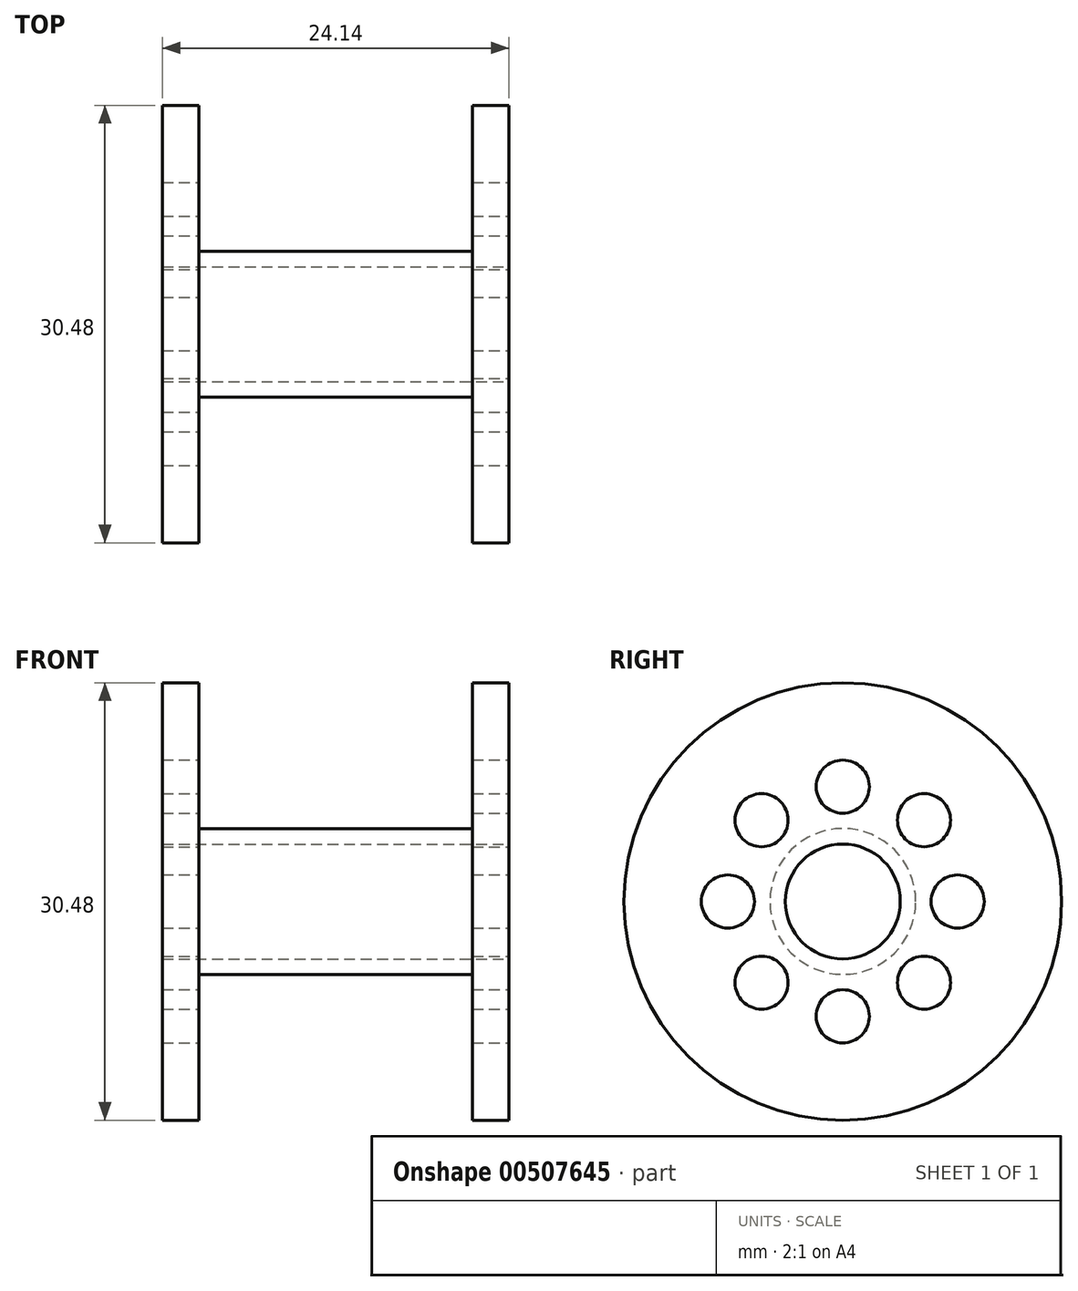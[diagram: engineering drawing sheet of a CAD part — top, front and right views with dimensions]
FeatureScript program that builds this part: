
annotation { "Feature Type Name" : "Feature", "Feature Type Description" : "" }
export const myFeature = defineFeature(function(context is Context, id is Id, definition is map)
    precondition{}
    {
        {
            var Q0;
            Q0=qCreatedBy(makeId("Top.planeOp"),FACE);
            var sketch = newSketch(context, id + "F0", { "sketchPlane" : qUnion([Q0])});
            skLineSegment(sketch, "E0.bottom", {"start": v(-9.53, 5.08) * mm, "end": v(9.53, 5.08) * mm});
            skLineSegment(sketch, "E0.left", {"start": v(-9.53, 5.08) * mm, "end": v(-9.53, 0) * mm});
            skLineSegment(sketch, "E0.right", {"start": v(9.53, 5.08) * mm, "end": v(9.53, 0) * mm});
            skPoint(sketch, "E0.middle", {"position": v(0, 0) * mm});
            skLineSegment(sketch, "E1.bottom", {"start": v(-9.53, 0) * mm, "end": v(-12.07, 0) * mm});
            skLineSegment(sketch, "E1.top", {"start": v(-9.53, 15.24) * mm, "end": v(-12.07, 15.24) * mm});
            skLineSegment(sketch, "E1.left", {"start": v(-9.53, 5.08) * mm, "end": v(-9.53, 15.24) * mm});
            skLineSegment(sketch, "E1.right", {"start": v(-12.07, 0) * mm, "end": v(-12.07, 15.24) * mm});
            skLineSegment(sketch, "E2.bottom", {"start": v(9.53, 0) * mm, "end": v(12.07, 0) * mm});
            skLineSegment(sketch, "E2.top", {"start": v(9.53, 15.24) * mm, "end": v(12.06, 15.24) * mm});
            skLineSegment(sketch, "E2.left", {"start": v(9.53, 0) * mm, "end": v(9.53, 15.24) * mm});
            skLineSegment(sketch, "E2.right", {"start": v(12.07, 0) * mm, "end": v(12.06, 15.24) * mm});
            skPoint(sketch, "E3.orphan", {"position": v(-9.52, -5.08) * mm});
            skPoint(sketch, "E4.orphan", {"position": v(9.53, -5.08) * mm});
            skLineSegment(sketch, "E5", {"start": v(-9.53, 0) * mm, "end": v(9.53, 0) * mm});
            skLineSegment(sketch, "E6", {"start": v(-9.53, 5.08) * mm, "end": v(-12.07, 5.08) * mm});
            skSolve(sketch);
        }
        {
            var Q0;
            {var subQ0=sQuery(id+"F0.wireOp",EDGE,"E1.top");Q0=makeQuery(id+"F0.imprint","IMPRINT",FACE,{"disambiguationData":[TD([[makeQuery(id+"F0.imprint","IMPRINT",EDGE,{"derivedFrom":subQ0}),1.0]])]});}
            var Q1;
            Q1=makeQuery(id+"F0.imprint","IMPRINT",FACE,{"disambiguationData":[TD([[makeQuery(id+"F0.imprint","IMPRINT",EDGE,{"derivedFrom":sQuery(id+"F0.wireOp",EDGE,"E0.left")}),-1.0]])]});
            var Q2;
            {var subQ0=sQuery(id+"F0.wireOp",EDGE,"E0.bottom");Q2=makeQuery(id+"F0.imprint","IMPRINT",FACE,{"disambiguationData":[TD([[makeQuery(id+"F0.imprint","IMPRINT",EDGE,{"derivedFrom":subQ0}),-1.0]])]});}
            var Q3;
            {var subQ3=sQuery(id+"F0.wireOp",EDGE,"E2.bottom");Q3=makeQuery(id+"F0.imprint","IMPRINT",FACE,{"disambiguationData":[TD([[makeQuery(id+"F0.imprint","IMPRINT",EDGE,{"derivedFrom":subQ3}),1.0]])]});}
            var Q4;
            Q4=sQuery(id+"F0.wireOp",EDGE,"E5");
            revolve(context, id + "F1", {"entities" : qUnion([Q0, Q1, Q2, Q3]), "axis" : qUnion([Q4]), "revolveType" : RevolveType.FULL});
        }
        {
            var Q0;
            Q0=makeQuery(id+"F1.opRevolve","SWEPT_FACE",FACE,{"disambiguationData":[OSD([sQuery(id+"F0.wireOp",EDGE,"E2.right")])]});
            var sketch = newSketch(context, id + "F2", { "sketchPlane" : qUnion([Q0])});
            skCircle(sketch, "E7", {"center": v(0, 0) * mm, "radius": 4 * mm});
            skCircle(sketch, "E8", {"center": v(0, 8) * mm, "radius": 1.85 * mm});
            skCircle(sketch, "E9.1.0", {"center": v(-5.66, 5.66) * mm, "radius": 1.85 * mm});
            skCircle(sketch, "E9.2.0", {"center": v(-8, 0) * mm, "radius": 1.85 * mm});
            skCircle(sketch, "E9.3.0", {"center": v(-5.66, -5.66) * mm, "radius": 1.85 * mm});
            skCircle(sketch, "E9.4.0", {"center": v(0, -8) * mm, "radius": 1.85 * mm});
            skCircle(sketch, "E9.5.0", {"center": v(5.66, -5.66) * mm, "radius": 1.85 * mm});
            skCircle(sketch, "E9.6.0", {"center": v(8, 0) * mm, "radius": 1.85 * mm});
            skCircle(sketch, "E9.7.0", {"center": v(5.66, 5.66) * mm, "radius": 1.85 * mm});
            skSolve(sketch);
        }
        {
            var Q0;
            Q0 = qSketchRegion(id + "F2", true);
            extrude(context, id + "F3", {"entities" : qUnion([Q0]), "operationType" : NewBodyOperationType.REMOVE, "oppositeDirection" : true, "depth" : 25.4 * mm});
        }
    });
